# Revit family: STS_10418_RV17_LOD400
name_source: partatom
category: Электрооборудование
revit_build: Autodesk Revit 2017 (Build: 20170118_1100(x64)
units: mm (PartAtom-declared; Revit-internal decimal feet)

## family parameters
Всегда вертикально = Да
Конфигурация панели = Два столбца, слева направо
На основе рабочей плоскости = Нет
Общий = Нет
При загрузке вырезать с полостями = Нет
Размер круглого соединителя = Использовать диаметр
Тип детали = Щит
Точка расчета площади = Нет

## types (2) — shared parameters
ADSK_URL страницы изделия = https://stilsoft.ru
ADSK_Единица измерения = шт.
ADSK_Завод-изготовитель = ООО «Основа Безопасности»
ADSK_Количество = 1
Диапазон рабочих температур, <unrecoverable-encoding: 5 bytes ef82b0d0a1> = от +5 до +50

## per-type parameters (varying)
| type | ADSK_Марка | ADSK_Масса | ADSK_Наименование | ADSK_Размер_Высота | ADSK_Размер_Глубина | ADSK_Размер_Ширина | высота, U |
| STS-10412 | СТВФ.426479.065 | 102 | Шкаф серверный защищенный STS-10412 | 1433 мм | 800 мм | 600 мм | 12 |
| STS-10418 | СТВФ.426479.067 | 80 | Шкаф серверный защищенный STS-10418 | 1031 мм | 805 мм | 610 мм | 18 |
